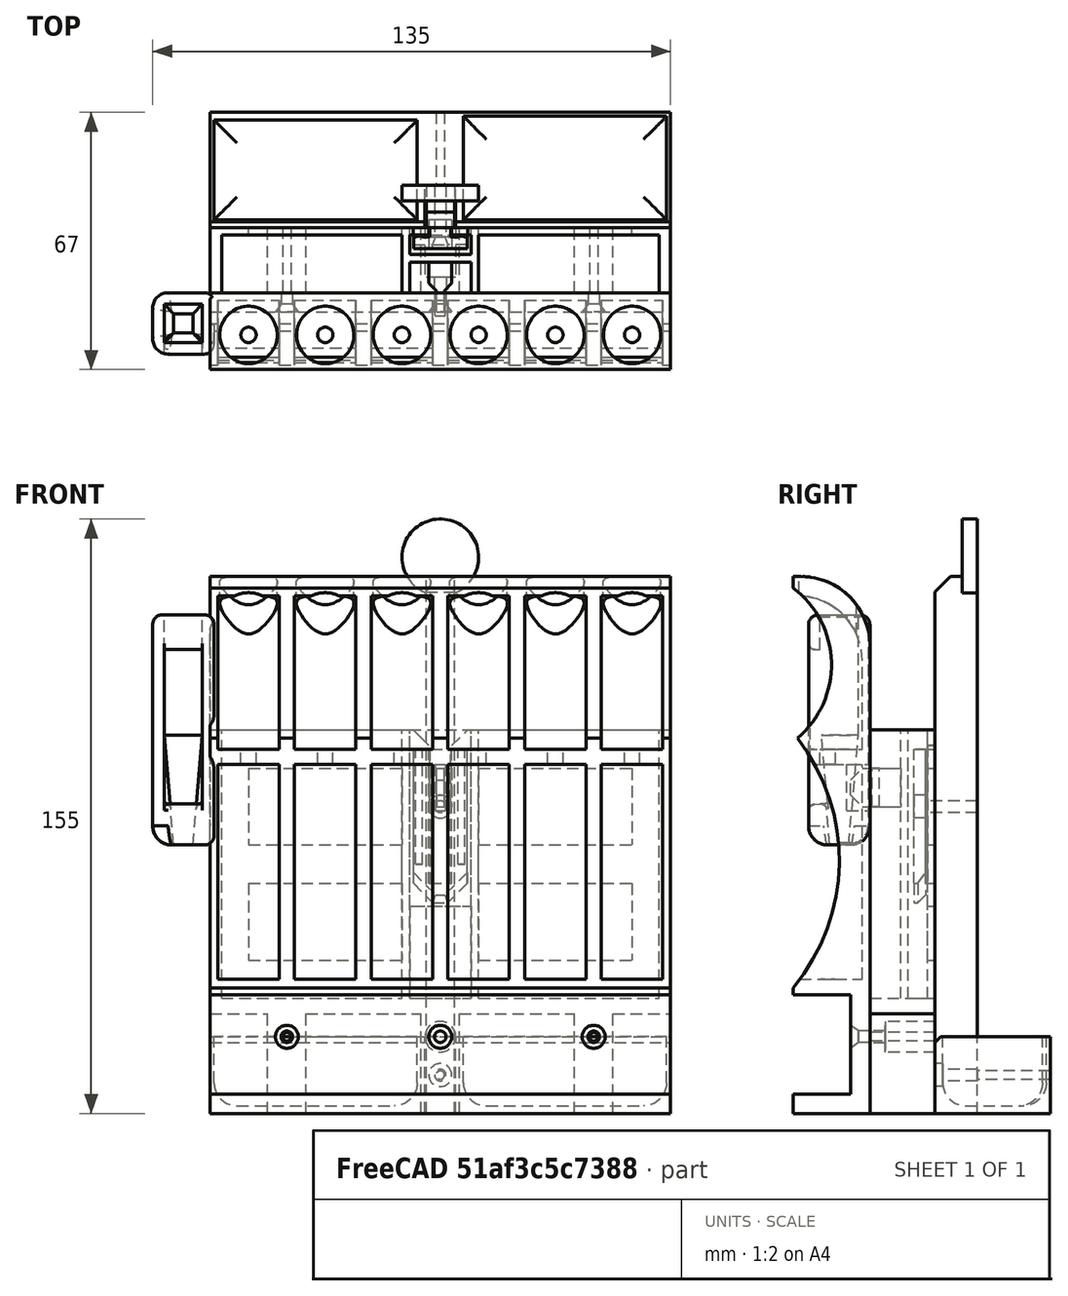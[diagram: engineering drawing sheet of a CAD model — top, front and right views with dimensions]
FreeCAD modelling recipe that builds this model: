
FCSTD DOCUMENT  (FreeCAD 0.18R16131 (Git))
Label: DrzacSrafcigera
License: All rights reserved
LicenseURL: http://en.wikipedia.org/wiki/All_rights_reserved
objects: Part::Box×31, Part::MultiFuse×23, Part::Cylinder×19, Part::Feature×6, Part::Cone×6, Part::Cut×6, Part::Chamfer×6, Part::Fillet×4
note: 101 computed .brp shape members not serialized (recipe doc carries the construction recipe); baked Part::Feature solids carry a one-line shape summary decoded from their .brp

FEATURE [Part::Box] Box  label="Cube"
  AttacherType = Attacher::AttachEngine3D
  Height = 140
  Length = 120
  Placement = pos=(-60,10,0) rot=(0,0,1;0rad)
  Width = 20
FEATURE [Part::Fillet] Fillet  label="MainMass"
  Base = -> Box
  Edges = 1 edges r=18: [Edge12]
FEATURE [Part::Box] Box003  label="Isecak"
  AttacherType = Attacher::AttachEngine3D
  Height = 26
  Length = 120
  Placement = pos=(-60,10,5) rot=(0,0,1;0rad)
  Width = 15
FEATURE [Part::Cylinder] Cylinder002  label="IsecakSrafcigera001"
  Angle = 360
  AttacherType = Attacher::AttachEngine3D
  Height = 90
  Placement = pos=(-50,19,95) rot=(0,0,1;0rad)
  Radius = 7.5
FEATURE [Part::Cylinder] Cylinder003  label="IsecakOsovine001"
  Angle = 360
  AttacherType = Attacher::AttachEngine3D
  Height = 60
  Placement = pos=(-50,19,35) rot=(0,0,1;0rad)
  Radius = 2
FEATURE [Part::Box] Box004  label="IsecakDMase001"
  AttacherType = Attacher::AttachEngine3D
  Height = 56
  Length = 16
  Placement = pos=(-58,10,35) rot=(0,0,1;0rad)
  Width = 18
FEATURE [Part::Box] Box006  label="IsecakGMase002"
  AttacherType = Attacher::AttachEngine3D
  Height = 40
  Length = 16
  Placement = pos=(-58,10,95) rot=(0,0,1;0rad)
  Width = 18
FEATURE [Part::Fillet] Fillet001
  Base = -> Box006
  Edges = 1 edges r=17: [Edge12]
FEATURE [Part::MultiFuse] Fusion002  label="Srafciger001"
  Shapes = -> [Fillet001,Cylinder003,Box004,Cylinder002]
FEATURE [Part::Feature] Fusion002001  label="Srafciger002"
  Placement = pos=(20,0,0) rot=(0,0,1;0rad)
  shape: bbox 16 x 18 x 150 mm, 18 faces (baked)
FEATURE [Part::Feature] Fusion002002  label="Srafciger003"
  Placement = pos=(40,0,0) rot=(0,0,1;0rad)
  shape: bbox 16 x 18 x 150 mm, 18 faces (baked)
FEATURE [Part::Feature] Fusion002003  label="Srafciger004"
  Placement = pos=(60,0,0) rot=(0,0,1;0rad)
  shape: bbox 16 x 18 x 150 mm, 18 faces (baked)
FEATURE [Part::Feature] Fusion002004  label="Srafciger005"
  Placement = pos=(80,0,0) rot=(0,0,1;0rad)
  shape: bbox 16 x 18 x 150 mm, 18 faces (baked)
FEATURE [Part::Feature] Fusion002005  label="Srafciger006"
  Placement = pos=(100,0,0) rot=(0,0,1;0rad)
  shape: bbox 16 x 18 x 150 mm, 18 faces (baked)
FEATURE [Part::MultiFuse] Fusion002006  label="SrafcigerIsecci"
  Shapes = -> [Fusion002,Fusion002004,Fusion002003,Fusion002002,Fusion002001,Fusion002005]
FEATURE [Part::Cylinder] Cylinder004  label="Cylinder"
  Angle = 360
  AttacherType = Attacher::AttachEngine3D
  Height = 120
  Placement = pos=(-60,-30,66) rot=(0,1,0;1.5708rad)
  Radius = 52
FEATURE [Part::Cylinder] Cylinder005  label="Cylinder001"
  Angle = 360
  AttacherType = Attacher::AttachEngine3D
  Height = 120
  Placement = pos=(-60,-5,117) rot=(0,1,0;1.5708rad)
  Radius = 25
FEATURE [Part::Cone] Cone  label="KonusSrafaKutije001"
  Angle = 360
  AttacherType = Attacher::AttachEngine3D
  Height = 2
  Placement = pos=(0,0,0) rot=(1,0,0;1.5708rad)
  Radius1 = 1.5
  Radius2 = 3
FEATURE [Part::Cylinder] Cylinder006  label="RupaSrafaKutije001"
  Angle = 360
  AttacherType = Attacher::AttachEngine3D
  Height = 10
  Placement = pos=(0,10,0) rot=(1,0,0;1.5708rad)
  Radius = 1.5
FEATURE [Part::MultiFuse] Fusion002009  label="Sraf001"
  Placement = pos=(-40,27,20) rot=(0,0,1;0rad)
  Shapes = -> [Cone,Cylinder006]
FEATURE [Part::Cylinder] Cylinder007  label="RupaSrafaKutije002"
  Angle = 360
  AttacherType = Attacher::AttachEngine3D
  Height = 10
  Placement = pos=(0,10,0) rot=(1,0,0;1.5708rad)
  Radius = 1.5
FEATURE [Part::Cone] Cone001  label="KonusSrafaKutije002"
  Angle = 360
  AttacherType = Attacher::AttachEngine3D
  Height = 2
  Placement = pos=(0,0,0) rot=(1,0,0;1.5708rad)
  Radius1 = 1.5
  Radius2 = 3
FEATURE [Part::MultiFuse] Fusion002010  label="Sraf002"
  Placement = pos=(40,27,20) rot=(0,0,1;0rad)
  Shapes = -> [Cone001,Cylinder007]
FEATURE [Part::Cylinder] Cylinder008  label="RupaSrafaKutije003"
  Angle = 360
  AttacherType = Attacher::AttachEngine3D
  Height = 10
  Placement = pos=(0,10,0) rot=(1,0,0;1.5708rad)
  Radius = 1.5
FEATURE [Part::Cone] Cone002  label="KonusSrafaKutije003"
  Angle = 360
  AttacherType = Attacher::AttachEngine3D
  Height = 2
  Placement = pos=(0,0,0) rot=(1,0,0;1.5708rad)
  Radius1 = 1.5
  Radius2 = 3
FEATURE [Part::MultiFuse] Fusion002011  label="Sraf003"
  Placement = pos=(0,27,20) rot=(0,0,1;0rad)
  Shapes = -> [Cone002,Cylinder008]
FEATURE [Part::MultiFuse] Fusion002012  label="Srafovi"
  Shapes = -> [Fusion002009,Fusion002011,Fusion002010]
FEATURE [Part::MultiFuse] Fusion002013  label="Rupe001"
  Shapes = -> [Cylinder005,Cylinder004,Fusion002012]
FEATURE [Part::Cylinder] Cylinder009  label="RupaSrafaKutije004"
  Angle = 360
  AttacherType = Attacher::AttachEngine3D
  Height = 20
  Placement = pos=(0,20,0) rot=(1,0,0;1.5708rad)
  Radius = 1.1
FEATURE [Part::Cylinder] Cylinder010  label="RupaSrafaKutije005"
  Angle = 360
  AttacherType = Attacher::AttachEngine3D
  Height = 20
  Placement = pos=(0,20,0) rot=(1,0,0;1.5708rad)
  Radius = 1.1
FEATURE [Part::Cylinder] Cylinder011  label="RupaSrafaKutije006"
  Angle = 360
  AttacherType = Attacher::AttachEngine3D
  Height = 20
  Placement = pos=(0,20,0) rot=(1,0,0;1.5708rad)
  Radius = 1.6
FEATURE [Part::Cone] Cone003  label="KonusSrafaKutije004"
  Angle = 360
  AttacherType = Attacher::AttachEngine3D
  Height = 2
  Placement = pos=(0,0,0) rot=(1,0,0;1.5708rad)
  Radius1 = 1.5
  Radius2 = 3
FEATURE [Part::Cone] Cone004  label="KonusSrafaKutije005"
  Angle = 360
  AttacherType = Attacher::AttachEngine3D
  Height = 3
  Placement = pos=(0,17,0) rot=(1,0,0;1.5708rad)
  Radius1 = 4
  Radius2 = 1
FEATURE [Part::MultiFuse] Fusion002015  label="Sraf004"
  Placement = pos=(0,30,20) rot=(0,0,1;0rad)
  Shapes = -> [Cone004,Cylinder011]
FEATURE [Part::Cone] Cone005  label="KonusSrafaKutije006"
  Angle = 360
  AttacherType = Attacher::AttachEngine3D
  Height = 2
  Placement = pos=(0,0,0) rot=(1,0,0;1.5708rad)
  Radius1 = 1.5
  Radius2 = 3
FEATURE [Part::MultiFuse] Fusion002016  label="Sraf005"
  Placement = pos=(40,27,20) rot=(0,0,1;0rad)
  Shapes = -> [Cone003,Cylinder009]
FEATURE [Part::MultiFuse] Fusion002017  label="Sraf006"
  Placement = pos=(-40,27,20) rot=(0,0,1;0rad)
  Shapes = -> [Cone005,Cylinder010]
FEATURE [Part::Box] Box007  label="MasaDrzacaKljesta"
  AttacherType = Attacher::AttachEngine3D
  Height = 100
  Length = 120
  Placement = pos=(-60,30,0) rot=(0,0,1;0rad)
  Width = 17
FEATURE [Part::Box] Box008  label="Supljina001"
  AttacherType = Attacher::AttachEngine3D
  Height = 70
  Length = 47
  Placement = pos=(-57,30,30) rot=(0,0,1;0rad)
  Width = 15
FEATURE [Part::Box] Box009  label="Supljina004"
  AttacherType = Attacher::AttachEngine3D
  Height = 26
  Length = 30
  Placement = pos=(5,30,0) rot=(0,0,1;0rad)
  Width = 20
FEATURE [Part::Box] Box010  label="Supljina005"
  AttacherType = Attacher::AttachEngine3D
  Height = 26
  Length = 30
  Placement = pos=(-35,30,0) rot=(0,0,1;0rad)
  Width = 20
FEATURE [Part::Box] Box011  label="Supljina007"
  AttacherType = Attacher::AttachEngine3D
  Height = 26
  Length = 30
  Placement = pos=(45,30,0) rot=(0,0,1;0rad)
  Width = 20
FEATURE [Part::Box] Box012  label="Supljina006"
  AttacherType = Attacher::AttachEngine3D
  Height = 26
  Length = 30
  Placement = pos=(-75,30,0) rot=(0,0,1;0rad)
  Width = 20
FEATURE [Part::Box] Box013  label="Supljina002"
  AttacherType = Attacher::AttachEngine3D
  Height = 20
  Length = 40
  Placement = pos=(-50,40,40) rot=(0,0,1;0rad)
  Width = 15
FEATURE [Part::Box] Box014  label="Supljina003"
  AttacherType = Attacher::AttachEngine3D
  Height = 20
  Length = 40
  Placement = pos=(-50,40,70) rot=(0,0,1;0rad)
  Width = 15
FEATURE [Part::Box] Box015  label="MasaKlizaca"
  AttacherType = Attacher::AttachEngine3D
  Height = 70
  Length = 16
  Placement = pos=(-8,40,30) rot=(0,0,1;0rad)
  Width = 5
FEATURE [Part::Box] Box016  label="RupaKlizaca002"
  AttacherType = Attacher::AttachEngine3D
  Height = 70
  Length = 14
  Placement = pos=(-7,47,30) rot=(0,0,1;0rad)
  Width = 4
FEATURE [Part::Box] Box017  label="RupaKlizaca001"
  AttacherType = Attacher::AttachEngine3D
  Height = 70
  Length = 6
  Placement = pos=(-3,47,60) rot=(0,0,1;0rad)
  Width = 6
FEATURE [Part::Box] Box018  label="RupaKlizaca003"
  AttacherType = Attacher::AttachEngine3D
  Height = 10
  Length = 10
  Placement = pos=(-7.05,47,100) rot=(0,1,0;0.785398rad)
  Width = 6
FEATURE [Part::MultiFuse] Fusion002021
  Placement = pos=(0,-6,0) rot=(0,0,1;0rad)
  Shapes = -> [Box018,Box016,Box017]
FEATURE [Part::Box] Box020  label="Supljina008"
  AttacherType = Attacher::AttachEngine3D
  Height = 70
  Length = 47
  Placement = pos=(10,30,30) rot=(0,0,1;0rad)
  Width = 15
FEATURE [Part::Box] Box021  label="Supljina009"
  AttacherType = Attacher::AttachEngine3D
  Height = 20
  Length = 40
  Placement = pos=(10,40,70) rot=(0,0,1;0rad)
  Width = 15
FEATURE [Part::Box] Box022  label="Supljina010"
  AttacherType = Attacher::AttachEngine3D
  Height = 20
  Length = 40
  Placement = pos=(10,40,40) rot=(0,0,1;0rad)
  Width = 15
FEATURE [Part::Box] Box023  label="MasaKlizaca001"
  AttacherType = Attacher::AttachEngine3D
  Height = 70
  Length = 16
  Placement = pos=(-8,30,30) rot=(0,0,1;0rad)
  Width = 8
FEATURE [Part::MultiFuse] Fusion002022
  Shapes = -> [Box023,Box021,Box008,Fusion002021,Box015,Box009,Box010,Box013,Box012,Box011,Box014,Box022,Box020]
FEATURE [Part::Box] Box024  label="RupaKlizaca004"
  AttacherType = Attacher::AttachEngine3D
  Height = 24
  Length = 16
  Placement = pos=(-8,42,30) rot=(0,0,1;0rad)
  Width = 10
FEATURE [Part::Box] Box025  label="TeloFioke001"
  AttacherType = Attacher::AttachEngine3D
  Height = 20
  Length = 120
  Placement = pos=(-60,47,0) rot=(0,0,1;0rad)
  Width = 30
FEATURE [Part::Box] Box026  label="RupaFioke001"
  AttacherType = Attacher::AttachEngine3D
  Height = 20
  Length = 53
  Placement = pos=(-59,49,2) rot=(0,0,1;0rad)
  Width = 26
FEATURE [Part::Fillet] Fillet005002  label="Rupa001"
  Base = -> Box026
  Edges = 4 edges r=6: [Edge4,Edge8,Edge9,Edge11]
FEATURE [Part::Box] Box030  label="Drzac004"
  AttacherType = Attacher::AttachEngine3D
  Height = 100
  Length = 8
  Placement = pos=(-4,47,0) rot=(0,0,1;0rad)
  Width = 11
FEATURE [Part::Box] Box031  label="RupaFioke002"
  AttacherType = Attacher::AttachEngine3D
  Height = 20
  Length = 53
  Placement = pos=(6,49,2) rot=(0,0,1;0rad)
  Width = 27
FEATURE [Part::Fillet] Fillet005003  label="Rupa002"
  Base = -> Box031
  Edges = 4 edges r=6: [Edge4,Edge8,Edge9,Edge11]
FEATURE [Part::Box] Box032  label="TeloKlizaca"
  AttacherType = Attacher::AttachEngine3D
  Height = 140
  Length = 7.4
  Placement = pos=(-3.7,47,0) rot=(0,0,1;0rad)
  Width = 11
FEATURE [Part::MultiFuse] Fusion002023  label="RupeFioke"
  Shapes = -> [Fillet005003,Fillet005002]
FEATURE [Part::Cylinder] Cylinder012  label="RupaSrafa003"
  Angle = 360
  AttacherType = Attacher::AttachEngine3D
  Height = 30
  Placement = pos=(0,80,10) rot=(1,0,0;1.5708rad)
  Radius = 1.1
FEATURE [Part::MultiFuse] Fusion002024  label="SupljineFioke001"
  Shapes = -> [Fusion002023,Cylinder012,Box030]
FEATURE [Part::Cut] Cut004  label="FiokaTelo001"
  Base = -> Box025
  Tool = -> Fusion002024
FEATURE [Part::Chamfer] Chamfer  label="Fioka001"
  Base = -> Cut004
  Edges = 2 edges r=1.5: [Edge7,Edge10]
FEATURE [Part::Cylinder] Cylinder013  label="RupaSrafa004"
  Angle = 360
  AttacherType = Attacher::AttachEngine3D
  Height = 50
  Placement = pos=(0,80,10) rot=(1,0,0;1.5708rad)
  Radius = 1.5
FEATURE [Part::Cylinder] Cylinder014  label="RupaSrafa005"
  Angle = 360
  AttacherType = Attacher::AttachEngine3D
  Height = 50
  Placement = pos=(0,80,80) rot=(1,0,0;1.5708rad)
  Radius = 1.5
FEATURE [Part::Box] Box033  label="Klizac002"
  AttacherType = Attacher::AttachEngine3D
  Height = 35
  Length = 5.4
  Placement = pos=(-2.7,44.5,60) rot=(0,0,1;0rad)
  Width = 3
FEATURE [Part::Box] Box034  label="Klizac003"
  AttacherType = Attacher::AttachEngine3D
  Height = 40
  Length = 14
  Placement = pos=(-7,41.5,55) rot=(0,0,1;0rad)
  Width = 3
FEATURE [Part::Chamfer] Chamfer002
  Base = -> Box034
  Edges = 2 edges r=5: [Edge4,Edge8]
FEATURE [Part::Chamfer] Chamfer003
  Base = -> Chamfer002
  Edges = 3 edges r=2: [Edge11,Edge14,Edge15]
FEATURE [Part::Cylinder] Cylinder015  label="Cylinder002"
  Angle = 360
  AttacherType = Attacher::AttachEngine3D
  Height = 30
  Placement = pos=(5.5,43.3,65) rot=(0,0,1;0rad)
  Radius = 1.5
FEATURE [Part::Cylinder] Cylinder016  label="Cylinder003"
  Angle = 360
  AttacherType = Attacher::AttachEngine3D
  Height = 30
  Placement = pos=(-5.5,43.3,65) rot=(0,0,1;0rad)
  Radius = 1.5
FEATURE [Part::Cylinder] Cylinder017  label="Hvataljka"
  Angle = 360
  AttacherType = Attacher::AttachEngine3D
  Height = 4
  Placement = pos=(0,58,145) rot=(1,0,0;1.5708rad)
  Radius = 10
FEATURE [Part::Chamfer] Chamfer004
  Base = -> Box032
  Edges = 2 edges r=4: [Edge10,Edge12]
FEATURE [Part::Cylinder] Cylinder018  label="RupaSrafa006"
  Angle = 360
  AttacherType = Attacher::AttachEngine3D
  Height = 3
  Placement = pos=(0,44.5,80) rot=(1,0,0;1.5708rad)
  Radius = 3
FEATURE [Part::Cylinder] Cylinder019  label="RupaSrafa007"
  Angle = 360
  AttacherType = Attacher::AttachEngine3D
  Height = 2
  Placement = pos=(0,49,10) rot=(1,0,0;1.5708rad)
  Radius = 3
FEATURE [Part::MultiFuse] Fusion002025
  Shapes = -> [Chamfer003,Cylinder017,Chamfer004,Cylinder016,Cylinder015]
FEATURE [Part::MultiFuse] Fusion002026  label="MasaKlizaca002"
  Shapes = -> [Fusion002025,Box033]
FEATURE [Part::MultiFuse] Fusion002027  label="RupeKlizaca"
  Shapes = -> [Cylinder019,Cylinder013,Cylinder018,Cylinder014]
FEATURE [Part::Cut] Cut005  label="Klizac"
  Base = -> Fusion002026
  Tool = -> Fusion002027
FEATURE [Part::MultiFuse] Fusion  label="Supljine"
  Shapes = -> [Fusion002013,Fusion002006,Box003]
FEATURE [Part::Feature] Fillet005005001  label="DrzacPincete"
  shape: bbox 16.01 x 16.82 x 60.41 mm, 59 faces (baked)
FEATURE [Part::Cut] Cut
  Base = -> Fillet
  Tool = -> Fusion
FEATURE [Part::MultiFuse] Fusion002028  label="DrzacSrafcigeraMasa"
  Shapes = -> [Fillet005005001,Cut]
FEATURE [Part::Cylinder] Cylinder020  label="RupaSrafaKutije007"
  Angle = 360
  AttacherType = Attacher::AttachEngine3D
  Height = 13
  Placement = pos=(0,47,20) rot=(1,0,0;1.5708rad)
  Radius = 4
FEATURE [Part::MultiFuse] Fusion002029
  Shapes = -> [Fusion002015,Cylinder020]
FEATURE [Part::MultiFuse] Fusion002030  label="RupeSrafova"
  Shapes = -> [Fusion002029,Fusion002016,Fusion002017]
FEATURE [Part::Box] Box035  label="Cube001"
  AttacherType = Attacher::AttachEngine3D
  Height = 10
  Length = 2
  Placement = pos=(-1,25,80) rot=(0,0,1;0rad)
  Width = 15
FEATURE [Part::Box] Box036  label="Cube002"
  AttacherType = Attacher::AttachEngine3D
  Height = 10
  Length = 6
  Placement = pos=(-3,30.5,80) rot=(0,0,1;0rad)
  Width = 8
FEATURE [Part::Chamfer] Chamfer005
  Base = -> Box035
  Edges = 2 edges r=3: [Edge9,Edge10]
FEATURE [Part::Box] Box037  label="Cube003"
  AttacherType = Attacher::AttachEngine3D
  Height = 12
  Length = 2.6
  Placement = pos=(-1.3,24,79) rot=(0,0,1;0rad)
  Width = 15
FEATURE [Part::Cut] Cut007  label="DrzacSrafcigera"
  Base = -> Fusion002028
  Tool = -> Box037
FEATURE [Part::Chamfer] Chamfer006
  Base = -> Box036
  Edges = 2 edges r=2: [Edge1,Edge5]
FEATURE [Part::Cut] Cut001
  Base = -> Box007
  Tool = -> Fusion002022
FEATURE [Part::MultiFuse] Fusion002031  label="MasaDrzaca"
  Shapes = -> [Cut001,Chamfer006,Chamfer005]
FEATURE [Part::MultiFuse] Fusion002032  label="Supljine001"
  Shapes = -> [Box024,Fusion002030]
FEATURE [Part::Cut] Cut008  label="DržačSečica"
  Base = -> Fusion002031
  Tool = -> Fusion002032
